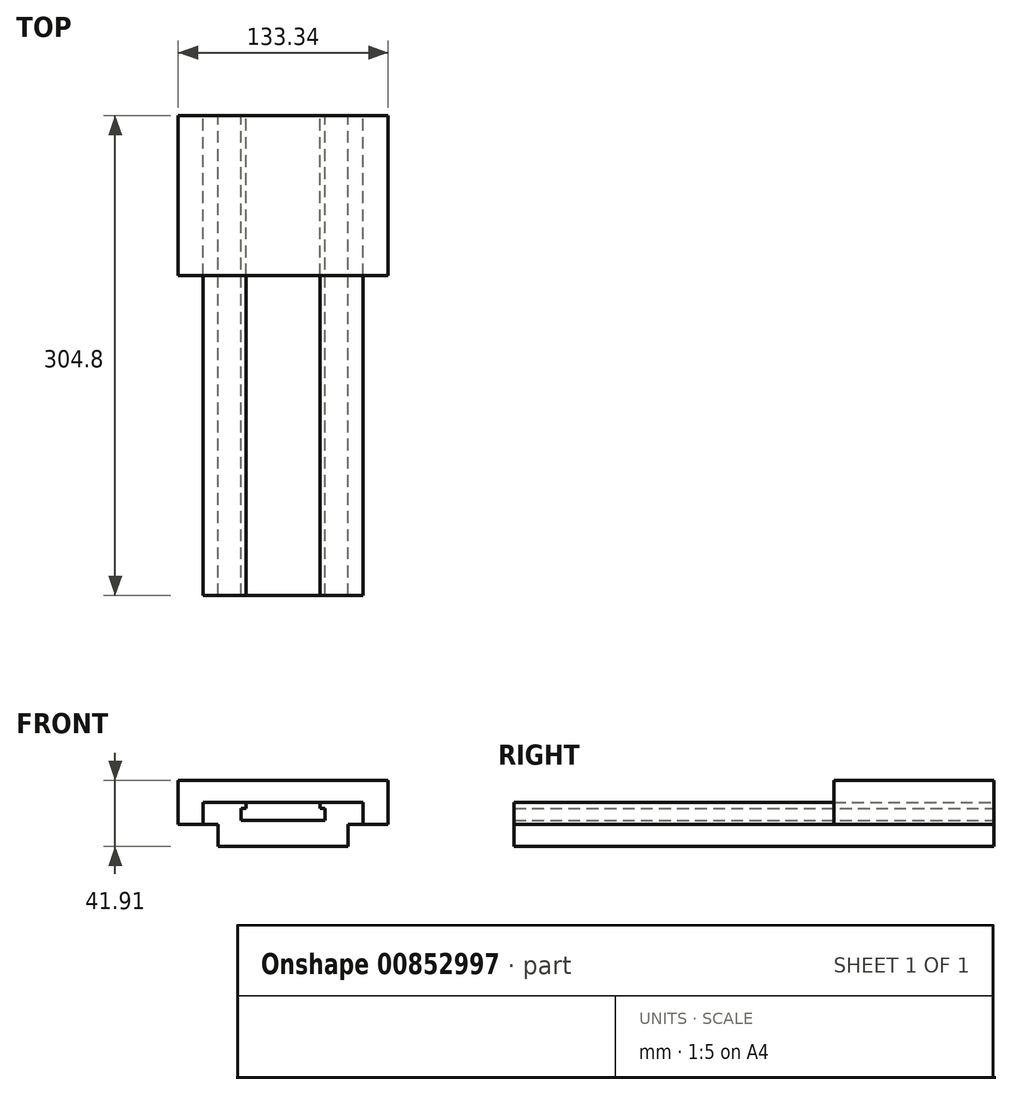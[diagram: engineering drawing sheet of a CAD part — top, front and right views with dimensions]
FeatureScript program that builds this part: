
annotation { "Feature Type Name" : "Feature", "Feature Type Description" : "" }
export const myFeature = defineFeature(function(context is Context, id is Id, definition is map)
    precondition{}
    {
        {
            var Q0;
            Q0=qCreatedBy(makeId("Front.planeOp"),FACE);
            var sketch = newSketch(context, id + "F0", { "sketchPlane" : qUnion([Q0])});
            skLineSegment(sketch, "E0", {"start": v(0, 16.51) * mm, "end": v(26.67, 16.51) * mm});
            skLineSegment(sketch, "E1", {"start": v(26.67, 16.5) * mm, "end": v(26.67, 24.13) * mm});
            skLineSegment(sketch, "E2", {"start": v(26.67, 24.13) * mm, "end": v(23.56, 24.13) * mm});
            skLineSegment(sketch, "E3", {"start": v(23.56, 24.13) * mm, "end": v(23.56, 27.94) * mm});
            skLineSegment(sketch, "E4", {"start": v(23.56, 27.94) * mm, "end": v(50.8, 27.94) * mm});
            skLineSegment(sketch, "E5", {"start": v(50.8, 27.94) * mm, "end": v(50.8, 13.97) * mm});
            skLineSegment(sketch, "E6", {"start": v(50.8, 13.97) * mm, "end": v(41.28, 13.97) * mm});
            skLineSegment(sketch, "E7", {"start": v(41.28, 13.97) * mm, "end": v(41.28, 0) * mm});
            skLineSegment(sketch, "E8", {"start": v(41.28, 0) * mm, "end": v(0, 0) * mm});
            skLineSegment(sketch, "E9.MirrorCS", {"start": v(0, 16.51) * mm, "end": v(-26.67, 16.5) * mm});
            skLineSegment(sketch, "E10.MirrorCS", {"start": v(-41.28, 0) * mm, "end": v(0, 0) * mm});
            skLineSegment(sketch, "E11.MirrorCS", {"start": v(-41.28, 13.97) * mm, "end": v(-41.28, 0) * mm});
            skLineSegment(sketch, "E12.MirrorCS", {"start": v(-50.8, 13.97) * mm, "end": v(-41.28, 13.97) * mm});
            skLineSegment(sketch, "E13.MirrorCS", {"start": v(-50.8, 27.94) * mm, "end": v(-50.8, 13.97) * mm});
            skLineSegment(sketch, "E14.MirrorCS", {"start": v(-23.56, 27.94) * mm, "end": v(-50.8, 27.94) * mm});
            skLineSegment(sketch, "E15.MirrorCS", {"start": v(-23.56, 24.13) * mm, "end": v(-23.56, 27.94) * mm});
            skLineSegment(sketch, "E16.MirrorCS", {"start": v(-26.67, 24.13) * mm, "end": v(-23.56, 24.13) * mm});
            skLineSegment(sketch, "E17.MirrorCS", {"start": v(-26.67, 16.5) * mm, "end": v(-26.67, 24.13) * mm});
            skLineSegment(sketch, "E18", {"start": v(23.56, 27.94) * mm, "end": v(0, 27.94) * mm});
            skLineSegment(sketch, "E19", {"start": v(0, 41.9) * mm, "end": v(66.68, 41.9) * mm});
            skLineSegment(sketch, "E20", {"start": v(66.68, 41.9) * mm, "end": v(66.68, 13.97) * mm});
            skLineSegment(sketch, "E21", {"start": v(66.68, 13.97) * mm, "end": v(50.8, 13.97) * mm});
            skLineSegment(sketch, "E22", {"start": v(66.68, 13.97) * mm, "end": v(66.68, 1.27) * mm});
            skLineSegment(sketch, "E23", {"start": v(66.68, 1.27) * mm, "end": v(41.28, 1.27) * mm});
            skLineSegment(sketch, "E24.MirrorCS", {"start": v(0, 41.9) * mm, "end": v(-66.68, 41.9) * mm});
            skLineSegment(sketch, "E25.MirrorCS", {"start": v(-23.56, 27.94) * mm, "end": v(0, 27.94) * mm});
            skLineSegment(sketch, "E26.MirrorCS", {"start": v(-66.68, 41.9) * mm, "end": v(-66.68, 13.97) * mm});
            skLineSegment(sketch, "E27.MirrorCS", {"start": v(-66.68, 13.97) * mm, "end": v(-66.68, 1.27) * mm});
            skLineSegment(sketch, "E28.MirrorCS", {"start": v(-66.68, 1.27) * mm, "end": v(-41.28, 1.27) * mm});
            skLineSegment(sketch, "E29", {"start": v(-50.8, 13.97) * mm, "end": v(-66.68, 13.97) * mm});
            skSolve(sketch);
        }
        {
            var Q0;
            Q0=makeQuery(id+"F0.imprint","IMPRINT",FACE,{"disambiguationData":[TD([[makeQuery(id+"F0.imprint","IMPRINT",EDGE,{"derivedFrom":sQuery(id+"F0.wireOp",EDGE,"E0")}),-1.0]])]});
            extrude(context, id + "F1", {"entities" : qUnion([Q0]), "depth" : 304.8 * mm, "offsetDistance" : 25.4 * mm});
        }
        {
            var Q0;
            Q0=makeQuery(id+"F0.imprint","IMPRINT",FACE,{"disambiguationData":[TD([[makeQuery(id+"F0.imprint","IMPRINT",EDGE,{"derivedFrom":sQuery(id+"F0.wireOp",EDGE,"E4")}),1.0]])]});
            extrude(context, id + "F2", {"entities" : qUnion([Q0]), "depth" : 101.6 * mm, "offsetDistance" : 25.4 * mm});
        }
    });
